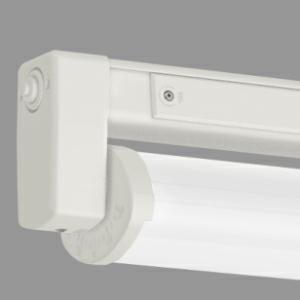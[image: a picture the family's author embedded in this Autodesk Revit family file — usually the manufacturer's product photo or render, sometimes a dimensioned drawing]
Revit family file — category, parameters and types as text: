
# Revit family: erfurt_led_extreme_m1500_-_5050lm___pmma_transopal_r___schlagzah__840_4000k__raumstrahlend_4336803421_0249
name_source: partatom
category: Lighting Fixtures
units: mm (PartAtom-declared; Revit-internal decimal feet)

## family parameters
Cut with Voids When Loaded = No
Host = Face
Light Source = No
Part Type = Normal
Room Calculation Point = No
Round Connector Dimension = Use Diameter
Shared = No

## types (1)
- ERFURT LED EXTREME m1500 - 5050lm , PMMA Transopal® (schlagzäh), 840/4000K, raumstrahlend (1 x LED Stripe, 5050 lm, 32 W, 840/4000K)
    Apparent Load = 35 VA
    Approval mark = CE, ENEC
    CIE Flux Codes = 56 85 96 98 98
    Color Rendering = 1B/80..89
    Color Temperature = 840/4000K
    Default Elevation = 1800 mm
    Description = Polymer luminaire for surface ceiling mounting with LED lamps, single or twin lamps. Useable in industrial applications and areas with special safety requirements. Long expected service life, useable up to +65 °C. Weather-proof and UV-resistant luminaire housing made of fibreglass-reinforced polymer, similar to RAL 9010. Useable for indoor and outdoor areas according to protection rating IP 65 (single or twin lamp). Thermally separated lamp chamber and driver chamber. Short sealing system consisting of age-resistant, form-retaining silicone/ synthetic rubber. Reflector tube with sealing system for easy LED replacement (easy eXchange LED). With reflector tubes that can be swivelled independently made of PMMA Transopal® (impact strengthened) or PC Tropal® (fracture proof) with internal aluminium reflector (MIRO-SILVER®). Reflector tube can be locked in increments of 10°. Luminaire ready for mounting and installation. Built-in driver 230 V AC/DC. Two cable entries M20 on face side and 4 x 1.5 mm² through wiring. Two access covers. L80 B10 > 100,000 h at +65 °C. 4 kV transient filter. 8 years manufacturer warranty. Single or row mounting. Ceiling or wall fixing using two stainless steel mounting clamps with variable mounting distance.


Length: 1551 mm
Width: 107 mm
Height: 140 mm
Weight: 4.6 kg

LOR: 97.7 %
    Height = 140 mm  [stored 0.459318 ft]
    Lamp = 1 x LED Stripe
    Lamp Light Flux = 5050 lm
    Lamp Power = 32 W
    Lamp count = 1
    Length = 1551 mm
    Lifetime = 100000 h
    Luminous efficacy = 141 lm/W
    Manufacturer = NORKA
    ModVariant = No
    Model = 4336803421
    Mounting Place = Ceiling, Wall
    Mounting Type = Surface mounted, Rail mounted
    Number of Poles = 1
    OnlyDefault = Yes
    Power Factor = 1
    Product Name = ERFURT LED EXTREME m1500 - 5050lm , PMMA Transopal® (schlagzäh), 840/4000K, raumstrahlend
    Product group = Ceiling-/wall luminaire
    ProductGroupID = 30
    Protection Class = Protection class II
    Protection Degree = IP 65
    RLX_Detail_Level = 1
    RlxData = <blob elided: 158717 chars, md5=8bbb01fc>
    Socket = socket
    Standby Power = 0 W
    System Light Flux = 4934 lm
    System Power = 35 W
    Type Comments = Product without accessories
    Type Image = erfurt-led-transopal.jpg
    URL = http://relux.com
    VarID = ---
    Voltage = 0 V
    Weight = 0.00 kg
    Width = 107 mm

note: [stored X ft] marks values corroborated as IEEE doubles in the binary element streams (Revit-internal decimal feet)

## geometry (parser evidence)
native form markers: Blend x4, Sweep x15
no freeform markers — native parametric forms only
